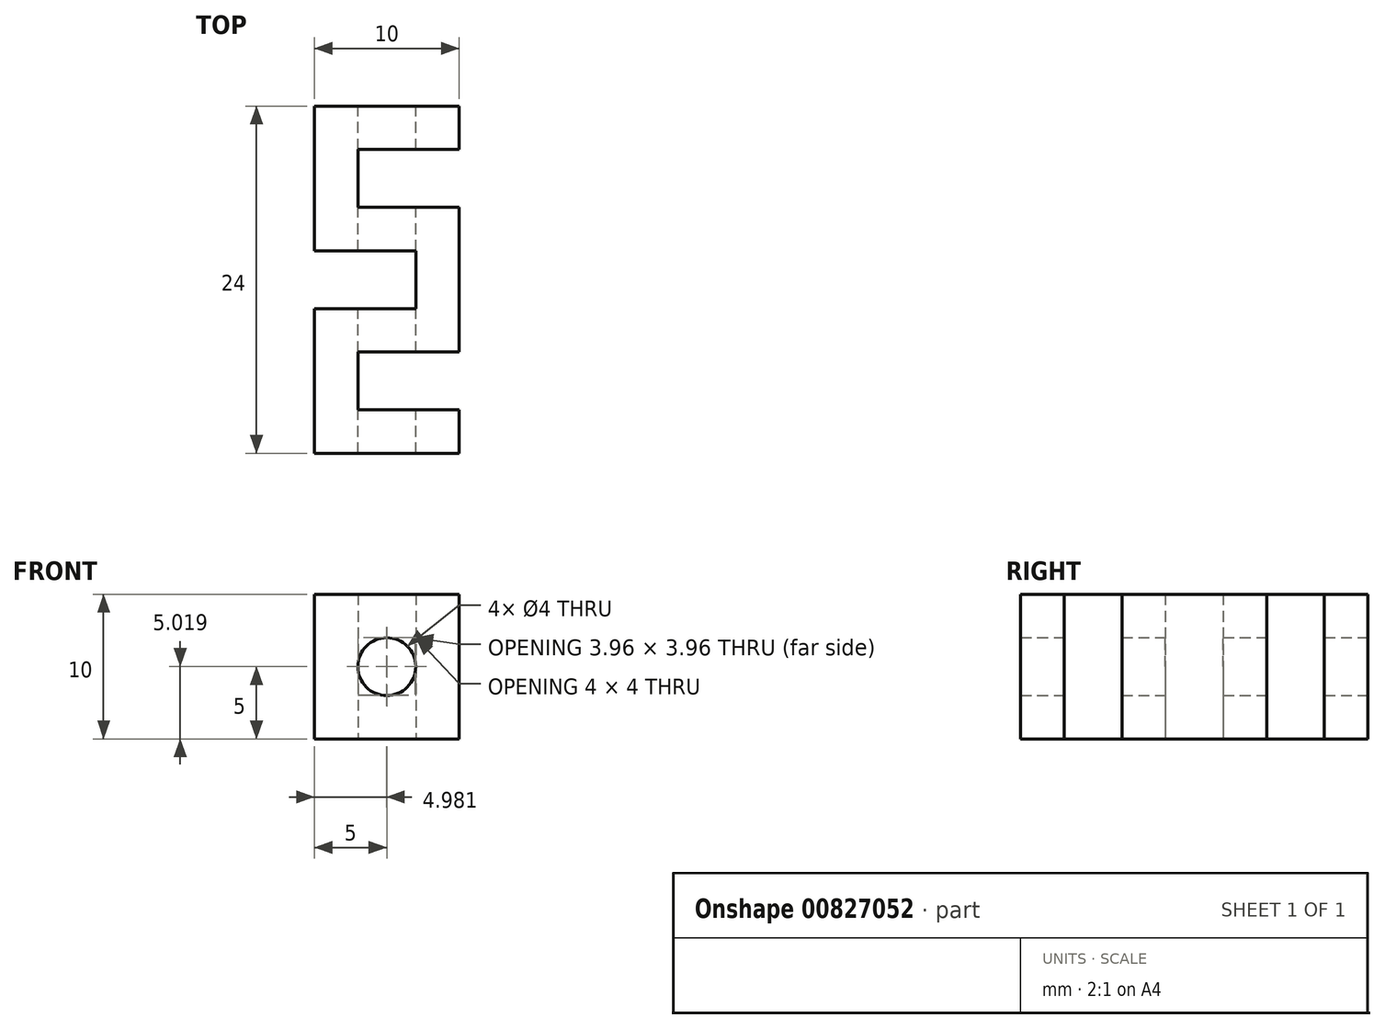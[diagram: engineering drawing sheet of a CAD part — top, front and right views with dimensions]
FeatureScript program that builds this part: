
annotation { "Feature Type Name" : "Feature", "Feature Type Description" : "" }
export const myFeature = defineFeature(function(context is Context, id is Id, definition is map)
    precondition{}
    {
        {
            var Q0;
            Q0=qCreatedBy(makeId("Top.planeOp"),FACE);
            var sketch = newSketch(context, id + "F0", { "sketchPlane" : qUnion([Q0])});
            skLineSegment(sketch, "E0", {"start": v(0, 0) * mm, "end": v(-10, 0) * mm});
            skLineSegment(sketch, "E1", {"start": v(-10, 0) * mm, "end": v(-10, -10) * mm});
            skLineSegment(sketch, "E2", {"start": v(-10, -10) * mm, "end": v(-3, -10) * mm});
            skLineSegment(sketch, "E3", {"start": v(-3, -10) * mm, "end": v(-3, -14) * mm});
            skLineSegment(sketch, "E4.0", {"start": v(0, -7) * mm, "end": v(0, -17) * mm});
            skLineSegment(sketch, "E4.1", {"start": v(-7, -7) * mm, "end": v(0, -7) * mm});
            skLineSegment(sketch, "E4.2", {"start": v(-7, -3) * mm, "end": v(-7, -7) * mm});
            skLineSegment(sketch, "E4.3", {"start": v(0, -3) * mm, "end": v(-7, -3) * mm});
            skLineSegment(sketch, "E5", {"start": v(0, 0) * mm, "end": v(0, -3) * mm});
            skLineSegment(sketch, "E6", {"start": v(-3, -14) * mm, "end": v(-10, -14) * mm});
            skLineSegment(sketch, "E7", {"start": v(-10, -14) * mm, "end": v(-10, -24) * mm});
            skLineSegment(sketch, "E8", {"start": v(-10, -24) * mm, "end": v(0, -24) * mm});
            skLineSegment(sketch, "E9", {"start": v(0, -24) * mm, "end": v(0, -21) * mm});
            skLineSegment(sketch, "E10", {"start": v(0, -21) * mm, "end": v(-7, -21) * mm});
            skLineSegment(sketch, "E11", {"start": v(-7, -21) * mm, "end": v(-7, -17) * mm});
            skLineSegment(sketch, "E12", {"start": v(-7, -17) * mm, "end": v(0, -17) * mm});
            skSolve(sketch);
        }
        {
            var Q0;
            Q0 = qSketchRegion(id + "F0", true);
            extrude(context, id + "F1", {"entities" : qUnion([Q0]), "depth" : 10 * mm, "offsetDistance" : 25 * mm});
        }
        {
            var Q0;
            Q0=makeQuery(id+"F1.opExtrude","SWEPT_FACE",FACE,{"disambiguationData":[OSD([sQuery(id+"F0.wireOp",EDGE,"E0")])]});
            var sketch = newSketch(context, id + "F2", { "sketchPlane" : qUnion([Q0])});
            skLineSegment(sketch, "E13", {"start": v(5, 0) * mm, "end": v(5, 10) * mm, "construction": true});
            skCircle(sketch, "E14", {"center": v(5, 5) * mm, "radius": 2 * mm});
            skSolve(sketch);
        }
        {
            var Q0;
            Q0=sQuery(id+"F2.wireOp",VERTEX,"E14.center");
            var Q1;
            Q1=makeQuery(id+"F1.opExtrude","SWEPT_BODY",BODY,{"disambiguationData":[OSD([sQuery(id+"F0.wireOp",EDGE,"E0"),sQuery(id+"F0.wireOp",EDGE,"E1"),sQuery(id+"F0.wireOp",EDGE,"E2"),sQuery(id+"F0.wireOp",EDGE,"E3"),sQuery(id+"F0.wireOp",EDGE,"E4.0"),sQuery(id+"F0.wireOp",EDGE,"E4.1"),sQuery(id+"F0.wireOp",EDGE,"E4.2"),sQuery(id+"F0.wireOp",EDGE,"E4.3"),sQuery(id+"F0.wireOp",EDGE,"E5"),sQuery(id+"F0.wireOp",EDGE,"E6"),sQuery(id+"F0.wireOp",EDGE,"E7"),sQuery(id+"F0.wireOp",EDGE,"E8"),sQuery(id+"F0.wireOp",EDGE,"E9"),sQuery(id+"F0.wireOp",EDGE,"E10"),sQuery(id+"F0.wireOp",EDGE,"E11"),sQuery(id+"F0.wireOp",EDGE,"E12")])]});
            hole(context, id + "F3", {"style" : HoleStyle.SIMPLE, "endStyle" : HoleEndStyle.THROUGH, "holeDiameter" : 4 * mm, "majorDiameter" : 5 * mm, "isTappedThrough" : true, "tappedDepth" : 12 * mm, "tapClearance" : 3, "locations" : qUnion([Q0]), "scope" : qUnion([Q1])});
        }
    });
